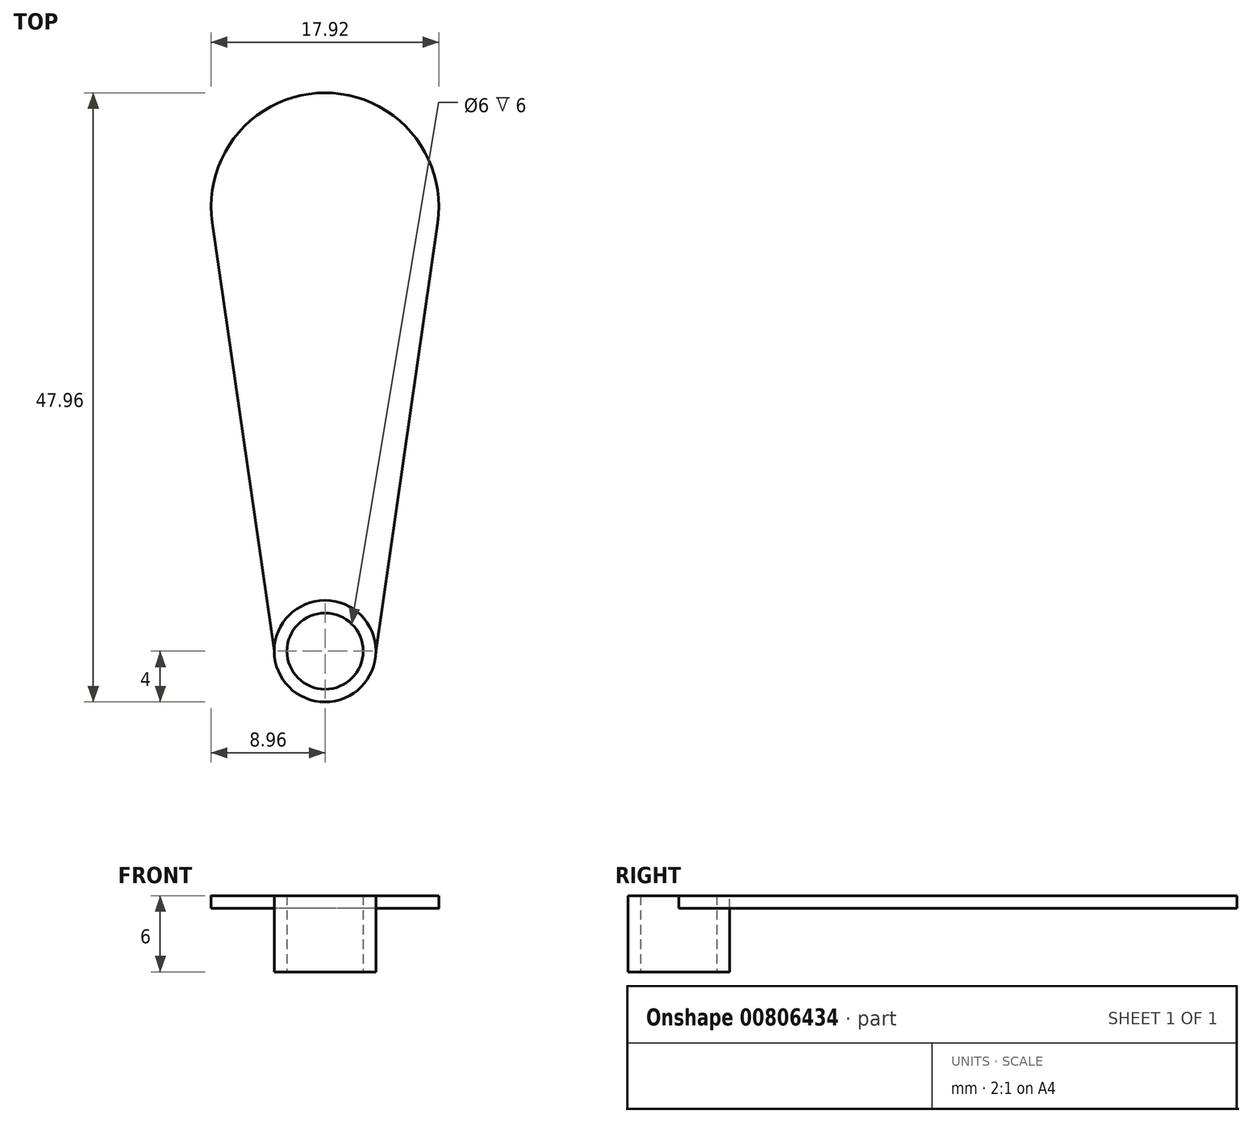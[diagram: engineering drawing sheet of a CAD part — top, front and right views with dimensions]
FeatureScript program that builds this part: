
annotation { "Feature Type Name" : "Feature", "Feature Type Description" : "" }
export const myFeature = defineFeature(function(context is Context, id is Id, definition is map)
    precondition{}
    {
        {
            var Q0;
            Q0=qCreatedBy(makeId("Top.planeOp"),FACE);
            var sketch = newSketch(context, id + "F0", { "sketchPlane" : qUnion([Q0])});
            skCircle(sketch, "E0", {"center": v(0, 0) * mm, "radius": 3 * mm});
            skCircle(sketch, "E1", {"center": v(0, 0) * mm, "radius": 4 * mm});
            skSolve(sketch);
        }
        {
            var Q0;
            Q0=makeQuery(id+"F0.imprint","IMPRINT",FACE,{"disambiguationData":[TD([[makeQuery(id+"F0.imprint","IMPRINT",EDGE,{"derivedFrom":sQuery(id+"F0.wireOp",EDGE,"E0")}),-1.0]])]});
            extrude(context, id + "F1", {"entities" : qUnion([Q0]), "depth" : 6 * mm, "offsetDistance" : 25.4 * mm});
        }
        {
            var Q0;
            Q0=makeQuery(id+"F1.opExtrude","CAP_FACE",FACE,{"disambiguationData":[OSD([sQuery(id+"F0.wireOp",EDGE,"E0"),sQuery(id+"F0.wireOp",EDGE,"E1")])],"isStart":false});
            var sketch = newSketch(context, id + "F2", { "sketchPlane" : qUnion([Q0])});
            skLineSegment(sketch, "E2", {"start": v(-4, 0) * mm, "end": v(-8.87, 33.72) * mm});
            skLineSegment(sketch, "E3", {"start": v(4, 0) * mm, "end": v(8.87, 33.72) * mm});
            skArc(sketch, "E4", {"start": v(-8.87, 33.72) * mm, "mid": v(0, 43.96) * mm, "end": v(8.87, 33.72) * mm});
            skSolve(sketch);
        }
        {
            var Q0;
            {var subQ0=sQuery(id+"F2.wireOp",EDGE,"E2");Q0=makeQuery(id+"F2.imprint","IMPRINT",FACE,{"disambiguationData":[TD([[makeQuery(id+"F2.imprint","IMPRINT",EDGE,{"derivedFrom":subQ0}),-1.0]])]});}
            var Q1;
            Q1=sQuery(id+"F2.wireOp",EDGE,"E3");
            var Q2;
            Q2=sQuery(id+"F2.wireOp",EDGE,"E2");
            var Q3;
            Q3=sQuery(id+"F2.wireOp",EDGE,"E4");
            extrude(context, id + "F3", {"entities" : qUnion([Q0]), "surfaceEntities" : qUnion([Q1, Q2, Q3]), "oppositeDirection" : true, "depth" : 1 * mm, "offsetDistance" : 25.4 * mm});
        }
    });
